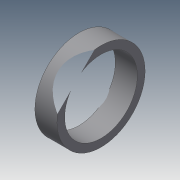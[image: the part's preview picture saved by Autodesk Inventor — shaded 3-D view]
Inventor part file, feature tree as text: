
AUTODESK INVENTOR PART (.ipt)
format: ipt  version: 2014 SP1 (Build 180222100, 222)  size: 235,008 bytes
history: native  units: in
note: dims shown in document units (in); Inventor stores cm internally (conversion verified against a paired STEP export)
features: sketch x4, other x3
ambient origin geometry x8: Origin, YZ Plane, XZ Plane, XY Plane, X Axis, Y Axis, Z Axis, Center Point
bodies: Solid1 (feature_tree)
feature tree (7):
  other  "Wheel.ipt"
  other  "Solid1::Wheel.ipt"
  other  "TaggingFeature1"
  sketch  "Sketch1"  dims[d0=0.3937in]
  sketch  "Sketch2"  dims[d1=0.5in d2=0.77in d3=1.5in d4=2.0in d5=2.5in d6=3.0in d7=3.3in d17=0.25in d18=0.0in d19=4.0in d20=0.5in d21=0.77in d22=1.5in d23=2.0in d24=2.5in d25=3.0in d26=3.3in d27=0.14in d28=0.14in d29=0.14in d30=0.14in d31=0.14in d32=1.0in d33=0.0in d34=4.0in d35=0.5in d36=0.77in d37=1.5in d38=2.0in d39=2.5in d40=3.0in d41=3.3in d42=0.14in d43=0.14in d44=0.14in d45=0.14in d46=0.14in d47=0.25in d48=0.0in d49=3.1496in d50=360.0deg d53=0.0625in d54=0.25in d55=0.0in d56=3.1496in d57=360.0deg]
  sketch  "Sketch4"
  sketch  "Sketch5"
